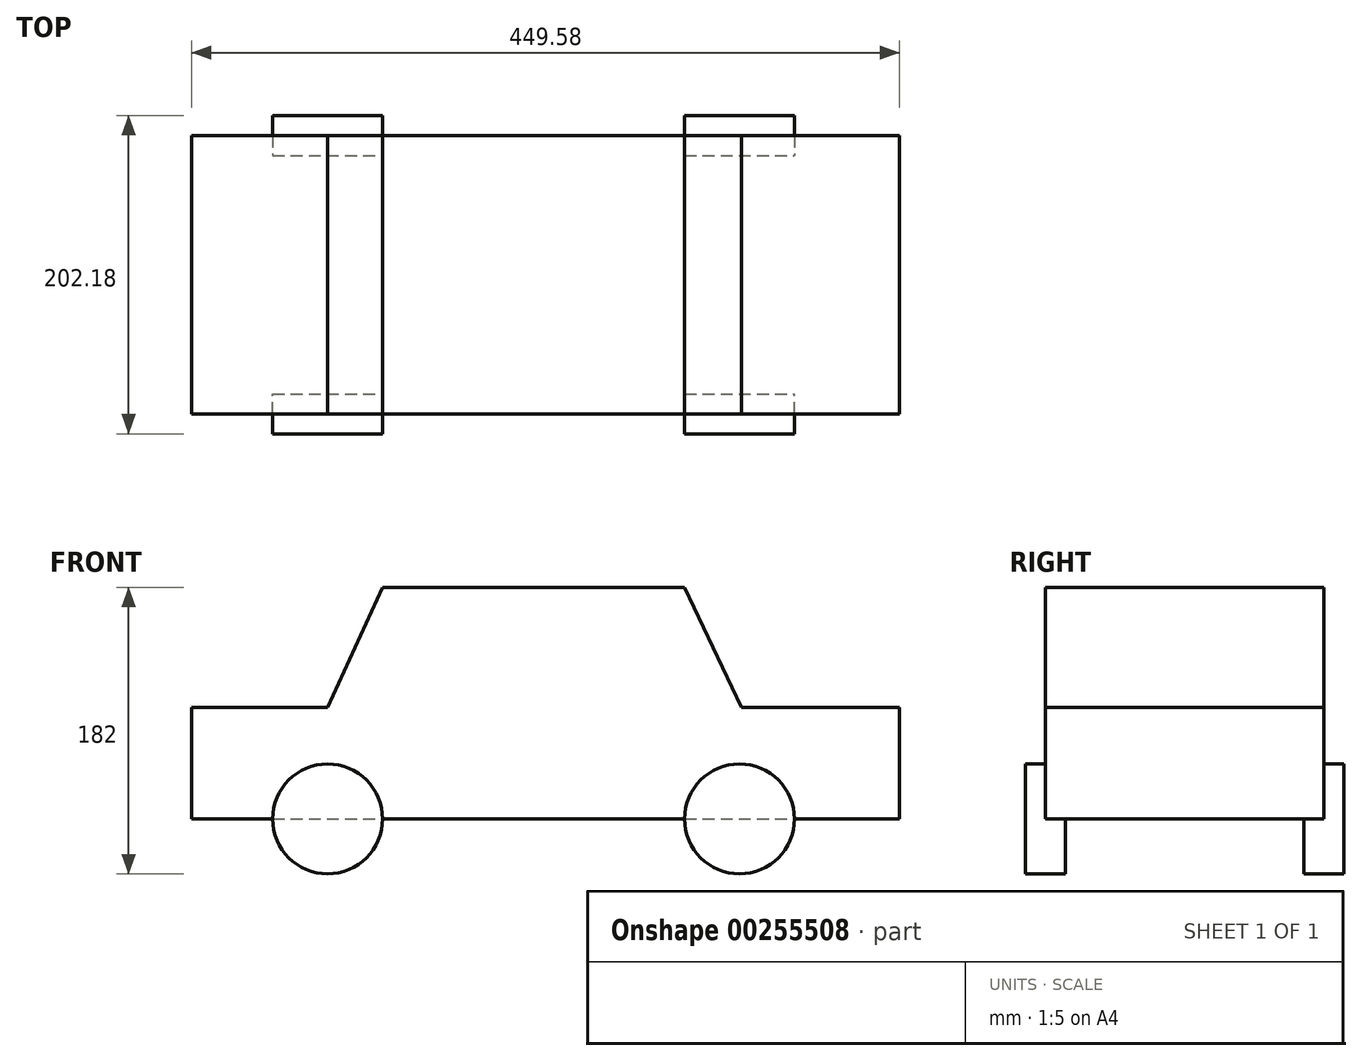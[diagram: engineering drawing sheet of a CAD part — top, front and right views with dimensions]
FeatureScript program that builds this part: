
annotation { "Feature Type Name" : "Feature", "Feature Type Description" : "" }
export const myFeature = defineFeature(function(context is Context, id is Id, definition is map)
    precondition{}
    {
        {
            var Q0;
            Q0=qCreatedBy(makeId("Top.planeOp"),FACE);
            var sketch = newSketch(context, id + "F0", { "sketchPlane" : qUnion([Q0])});
            skLineSegment(sketch, "E0.bottom", {"start": v(-220.7, 71.72) * mm, "end": v(228.88, 71.72) * mm});
            skLineSegment(sketch, "E0.top", {"start": v(-220.7, -105.06) * mm, "end": v(228.88, -105.06) * mm});
            skLineSegment(sketch, "E0.left", {"start": v(-220.7, 71.72) * mm, "end": v(-220.7, -105.06) * mm});
            skLineSegment(sketch, "E0.right", {"start": v(228.88, 71.72) * mm, "end": v(228.88, -105.06) * mm});
            skSolve(sketch);
        }
        {
            var Q0;
            Q0=makeQuery(id+"F0.imprint","IMPRINT",FACE,{"disambiguationData":[TD([[makeQuery(id+"F0.imprint","IMPRINT",EDGE,{"derivedFrom":sQuery(id+"F0.wireOp",EDGE,"E0.bottom")}),-1.0]])]});
            extrude(context, id + "F1", {"entities" : qUnion([Q0]), "depth" : 70.87 * mm});
        }
        {
            var Q0;
            Q0=makeQuery(id+"F1.opExtrude","SWEPT_FACE",FACE,{"disambiguationData":[OSD([sQuery(id+"F0.wireOp",EDGE,"E0.top")])]});
            var sketch = newSketch(context, id + "F2", { "sketchPlane" : qUnion([Q0])});
            skCircle(sketch, "E1", {"center": v(-134.34, 0) * mm, "radius": 34.93 * mm});
            skCircle(sketch, "E2", {"center": v(127.28, 0) * mm, "radius": 34.93 * mm});
            skSolve(sketch);
        }
        {
            var Q0;
            {var subQ0=sQuery(id+"F2.wireOp",EDGE,"E1");var subQ1=makeQuery(id+"F1.opExtrude","CAP_EDGE",EDGE,{"disambiguationData":[OSD([sQuery(id+"F0.wireOp",EDGE,"E0.top")])],"isStart":true});var subQ2=makeQuery(id+"F2.imprint","INTERSECT",VERTEX,{"disambiguationData":[OD(0.0)],"derivedFrom":[subQ1,subQ0]});Q0=makeQuery(id+"F2.imprint","IMPRINT",FACE,{"disambiguationData":[TD([[makeQuery(id+"F2.imprint","IMPRINT",EDGE,{"disambiguationData":[TD([[subQ2,-1.0]])],"derivedFrom":subQ0}),1.0]])]});}
            var Q1;
            {var subQ0=sQuery(id+"F2.wireOp",EDGE,"E1");var subQ1=makeQuery(id+"F1.opExtrude","CAP_EDGE",EDGE,{"disambiguationData":[OSD([sQuery(id+"F0.wireOp",EDGE,"E0.top")])],"isStart":true});var subQ2=makeQuery(id+"F2.imprint","INTERSECT",VERTEX,{"disambiguationData":[OD(0.0)],"derivedFrom":[subQ1,subQ0]});Q1=makeQuery(id+"F2.imprint","IMPRINT",FACE,{"disambiguationData":[TD([[makeQuery(id+"F2.imprint","IMPRINT",EDGE,{"disambiguationData":[TD([[subQ2,1.0]])],"derivedFrom":subQ0}),1.0]])]});}
            var Q2;
            {var subQ0=sQuery(id+"F2.wireOp",EDGE,"E2");var subQ1=makeQuery(id+"F1.opExtrude","CAP_EDGE",EDGE,{"disambiguationData":[OSD([sQuery(id+"F0.wireOp",EDGE,"E0.top")])],"isStart":true});var subQ2=makeQuery(id+"F2.imprint","INTERSECT",VERTEX,{"disambiguationData":[OD(0.0)],"derivedFrom":[subQ1,subQ0]});Q2=makeQuery(id+"F2.imprint","IMPRINT",FACE,{"disambiguationData":[TD([[makeQuery(id+"F2.imprint","IMPRINT",EDGE,{"disambiguationData":[TD([[subQ2,-1.0]])],"derivedFrom":subQ0}),1.0]])]});}
            var Q3;
            {var subQ0=sQuery(id+"F2.wireOp",EDGE,"E2");var subQ1=makeQuery(id+"F1.opExtrude","CAP_EDGE",EDGE,{"disambiguationData":[OSD([sQuery(id+"F0.wireOp",EDGE,"E0.top")])],"isStart":true});var subQ2=makeQuery(id+"F2.imprint","INTERSECT",VERTEX,{"disambiguationData":[OD(0.0)],"derivedFrom":[subQ1,subQ0]});Q3=makeQuery(id+"F2.imprint","IMPRINT",FACE,{"disambiguationData":[TD([[makeQuery(id+"F2.imprint","IMPRINT",EDGE,{"disambiguationData":[TD([[subQ2,1.0]])],"derivedFrom":subQ0}),1.0]])]});}
            extrude(context, id + "F3", {"entities" : qUnion([Q0, Q1, Q2, Q3]), "operationType" : NewBodyOperationType.ADD, "endBound" : BoundingType.SYMMETRIC, "depth" : 25.4 * mm});
        }
        {
            var Q0;
            Q0=makeQuery(id+"F1.opExtrude","SWEPT_FACE",FACE,{"disambiguationData":[OSD([sQuery(id+"F0.wireOp",EDGE,"E0.top")])]});
            cPlane(context, id + "F4", {"entities" : qUnion([Q0]), "cplaneType" : CPlaneType.OFFSET, "offset" : 88.4 * mm, "oppositeDirection" : true, "width" : 152.4 * mm, "height" : 152.4 * mm});
        }
        {
            var Q0;
            Q0=makeQuery(id+"F1.opExtrude","SWEPT_BODY",BODY,{"disambiguationData":[OSD([sQuery(id+"F0.wireOp",EDGE,"E0.bottom"),sQuery(id+"F0.wireOp",EDGE,"E0.top"),sQuery(id+"F0.wireOp",EDGE,"E0.left"),sQuery(id+"F0.wireOp",EDGE,"E0.right")])]});
            var Q1;
            Q1=qCreatedBy(id+"F4.planeOp",FACE);
            mirror(context, id + "F5", {"operationType" : NewBodyOperationType.ADD, "entities" : qUnion([Q0]), "mirrorPlane" : qUnion([Q1])});
        }
        {
            var Q0;
            Q0=makeQuery(id+"F1.opExtrude","CAP_FACE",FACE,{"disambiguationData":[OSD([sQuery(id+"F0.wireOp",EDGE,"E0.bottom"),sQuery(id+"F0.wireOp",EDGE,"E0.top"),sQuery(id+"F0.wireOp",EDGE,"E0.left"),sQuery(id+"F0.wireOp",EDGE,"E0.right")])],"isStart":false});
            var sketch = newSketch(context, id + "F6", { "sketchPlane" : qUnion([Q0])});
            skLineSegment(sketch, "E3.bottom", {"start": v(-134.47, 71.72) * mm, "end": v(128.66, 71.72) * mm});
            skLineSegment(sketch, "E3.top", {"start": v(-134.47, -105.06) * mm, "end": v(128.66, -105.06) * mm});
            skLineSegment(sketch, "E3.left", {"start": v(-134.47, 71.72) * mm, "end": v(-134.47, -105.06) * mm});
            skLineSegment(sketch, "E3.right", {"start": v(128.66, 71.72) * mm, "end": v(128.66, -105.06) * mm});
            skSolve(sketch);
        }
        {
            var Q0;
            Q0=makeQuery(id+"F6.imprint","IMPRINT",FACE,{"disambiguationData":[TD([[makeQuery(id+"F6.imprint","IMPRINT",EDGE,{"derivedFrom":sQuery(id+"F6.wireOp",EDGE,"E3.bottom")}),-1.0]])]});
            extrude(context, id + "F7", {"entities" : qUnion([Q0]), "operationType" : NewBodyOperationType.ADD, "depth" : 76.2 * mm});
        }
        {
            var Q0;
            Q0=makeQuery(id+"F7.boolean.opBoolean","MERGE",FACE,{"derivedFrom":[makeQuery(id+"F1.opExtrude","SWEPT_FACE",FACE,{"disambiguationData":[OSD([sQuery(id+"F0.wireOp",EDGE,"E0.top")])]}),makeQuery(id+"F7.opExtrude","SWEPT_FACE",FACE,{"disambiguationData":[OSD([sQuery(id+"F6.wireOp",EDGE,"E3.top")])]})]});
            var sketch = newSketch(context, id + "F8", { "sketchPlane" : qUnion([Q0])});
            skLineSegment(sketch, "E4", {"start": v(-134.47, 70.87) * mm, "end": v(-134.47, 147.07) * mm});
            skLineSegment(sketch, "E5", {"start": v(-134.47, 147.07) * mm, "end": v(-99.42, 147.07) * mm});
            skLineSegment(sketch, "E6", {"start": v(-99.42, 147.07) * mm, "end": v(-134.47, 70.87) * mm});
            skLineSegment(sketch, "E7", {"start": v(128.66, 70.87) * mm, "end": v(128.66, 147.07) * mm});
            skLineSegment(sketch, "E8", {"start": v(128.66, 147.07) * mm, "end": v(92.35, 147.07) * mm});
            skLineSegment(sketch, "E9", {"start": v(92.35, 147.07) * mm, "end": v(128.66, 70.87) * mm});
            skSolve(sketch);
        }
        {
            var Q0;
            Q0=makeQuery(id+"F8.imprint","IMPRINT",FACE,{"disambiguationData":[TD([[makeQuery(id+"F8.imprint","IMPRINT",EDGE,{"derivedFrom":sQuery(id+"F8.wireOp",EDGE,"E4")}),1.0]])]});
            var Q1;
            Q1=makeQuery(id+"F8.imprint","IMPRINT",FACE,{"disambiguationData":[TD([[makeQuery(id+"F8.imprint","IMPRINT",EDGE,{"derivedFrom":sQuery(id+"F8.wireOp",EDGE,"E7")}),-1.0]])]});
            extrude(context, id + "F9", {"entities" : qUnion([Q0, Q1]), "operationType" : NewBodyOperationType.REMOVE, "endBound" : BoundingType.THROUGH_ALL, "oppositeDirection" : true, "depth" : 25.4 * mm});
        }
    });
